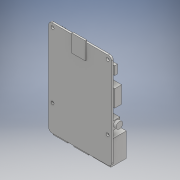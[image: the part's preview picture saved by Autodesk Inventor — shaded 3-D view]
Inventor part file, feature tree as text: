
AUTODESK INVENTOR PART (.ipt)
format: ipt  version: 2018 (Build 220112000, 112)  size: 447,488 bytes
history: native  units: mm
features: extrude x12, sketch x12
ambient origin geometry x8: Origin, YZ Plane, XZ Plane, XY Plane, X Axis, Y Axis, Z Axis, Center Point
bodies: Solid1 (feature_tree)
feature tree (24):
  extrude  "Extrusion1"  Depth=56.0mm
  extrude  "Extrusion2"  Depth=1.5748mm TaperAngle=0.0deg
  extrude  "Extrusion3"  Depth=3.5mm
  extrude  "Extrusion4"  Depth=3.5mm
  extrude  "Extrusion5"  Depth=3.5mm
  extrude  "Extrusion6"  Depth=3.5mm
  extrude  "Extrusion7"  Depth=0.7874mm TaperAngle=0.0deg
  extrude  "Extrusion8"  Depth=16.0mm
  extrude  "Extrusion9"  Depth=1.85mm
  extrude  "Extrusion10"  Depth=13.16mm
  extrude  "Extrusion11"  Depth=2.34mm
  extrude  "Extrusion12"  Depth=2.5mm
  sketch  "Sketch1"  dims[d0=3.0mm d1=56.0mm]
  sketch  "Sketch2"  dims[d2=85.0mm d3=1.5748mm d4=0.0mm]
  sketch  "Sketch3"  dims[d5=2.75mm d6=3.5mm]
  sketch  "Sketch4"  dims[d7=3.5mm d8=58.0mm]
  sketch  "Sketch5"  dims[d9=3.5mm d10=3.5mm]
  sketch  "Sketch6"  dims[d11=3.5mm d12=3.5mm]
  sketch  "Sketch7"  dims[d13=58.0mm d14=0.7874mm d15=0.0mm]
  sketch  "Sketch8"  dims[d16=21.2mm d17=16.0mm]
  sketch  "Sketch9"  dims[d18=10.25mm d19=1.85mm]
  sketch  "Sketch10"  dims[d20=13.82mm d21=0.0mm d22=13.16mm]
  sketch  "Sketch11"  dims[d23=17.65mm d24=2.34mm]
  sketch  "Sketch12"  dims[d25=35.0mm d26=2.5mm d27=15.0mm d28=0.0mm d30=3.5mm d31=50.8mm d32=5.08mm d33=29.0mm d34=2.54mm d35=0.0mm d36=0.65mm d37=1.71mm d38=1.71mm d39=200.0mm d41=2.54mm d42=20.0mm d44=2.54mm d47=5.92mm d48=0.0mm d49=1.8mm d50=1.8mm d51=2.6mm d52=4.0mm d53=2.2mm d54=6.2mm d55=11.15mm d56=0.0mm d57=10.6mm d58=5.6mm d59=7.6mm d60=1.2mm d61=2.44mm d62=0.0mm d63=32.0mm d64=15.0mm d65=11.0mm d66=1.25mm d67=6.17mm d68=0.0mm d69=7.26mm d70=12.5mm d71=53.5mm d72=5.84mm d73=0.0mm d74=5.9mm d75=2.46mm d76=0.0mm d77=12.0mm d78=15.5mm d79=13.2mm d80=34.0mm d81=1.4mm d82=0.0mm]
